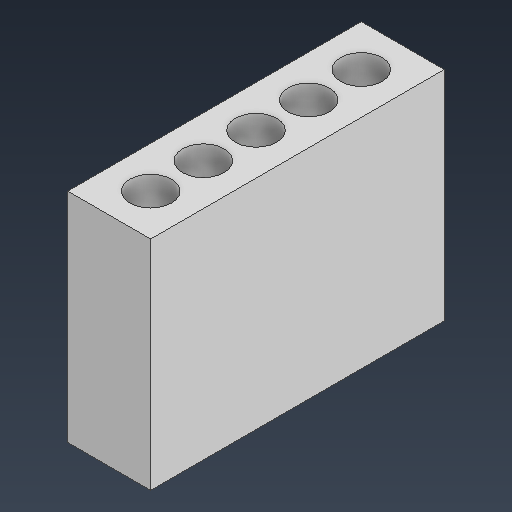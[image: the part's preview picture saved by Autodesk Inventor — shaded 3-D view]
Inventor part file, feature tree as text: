
AUTODESK INVENTOR PART (.ipt)
format: ipt  version: 2025.3 (Build 293356000, 356)  size: 111,104 bytes
history: native  units: mm
features: sketch x2, extrude x1
ambient origin geometry x8: Origin, YZ Plane, XZ Plane, XY Plane, X Axis, Y Axis, Z Axis, Center Point
bodies: Solid1 (feature_tree)
feature tree (3):
  extrude  "Extrusion1"  Depth=2.54mm
  sketch  "Sketch1"  dims[d0=2.0mm d1=50.0mm d3=2.54mm d4=10.0mm d6=10.0mm]
  sketch  "Sketch Rectangular Pattern1"  dims[d8=1.0mm d9=1.0mm d10=1.0mm d11=1.0mm d12=10.5mm d13=0.0mm]
